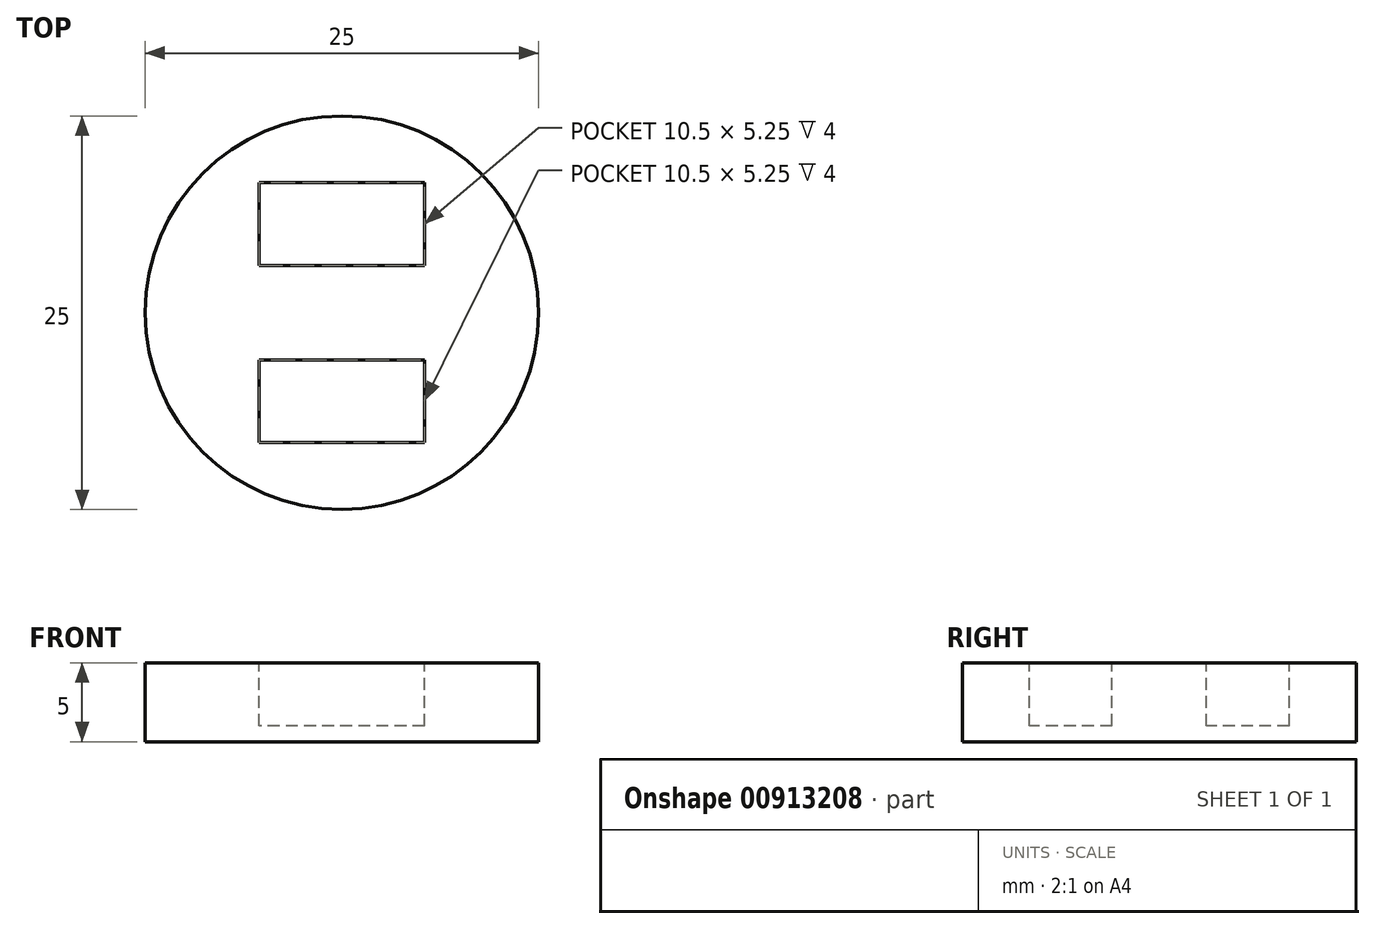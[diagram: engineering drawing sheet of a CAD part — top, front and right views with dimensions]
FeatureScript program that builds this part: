
annotation { "Feature Type Name" : "Feature", "Feature Type Description" : "" }
export const myFeature = defineFeature(function(context is Context, id is Id, definition is map)
    precondition{}
    {
        {
            var Q0;
            Q0=qCreatedBy(makeId("Top.planeOp"),FACE);
            var sketch = newSketch(context, id + "F0", { "sketchPlane" : qUnion([Q0])});
            skCircle(sketch, "E0", {"center": v(0, 0) * mm, "radius": 12.5 * mm});
            skSolve(sketch);
        }
        {
            var Q0;
            Q0=qSketchRegion(id+"F0",true);
            extrude(context, id + "F1", {"entities" : qUnion([Q0]), "depth" : 5 * mm, "offsetDistance" : 25 * mm});
        }
        {
            var Q0;
            Q0=makeQuery(id+"F1.opExtrude","CAP_FACE",FACE,{"disambiguationData":[OSD([sQuery(id+"F0.wireOp",EDGE,"E0")])],"isStart":false});
            var sketch = newSketch(context, id + "F2", { "sketchPlane" : qUnion([Q0])});
            skLineSegment(sketch, "E1.bottom", {"start": v(5.25, 8.25) * mm, "end": v(-5.25, 8.25) * mm});
            skLineSegment(sketch, "E1.top", {"start": v(5.25, 3) * mm, "end": v(-5.25, 3) * mm});
            skLineSegment(sketch, "E1.left", {"start": v(5.25, 8.25) * mm, "end": v(5.25, 3) * mm});
            skLineSegment(sketch, "E1.right", {"start": v(-5.25, 8.25) * mm, "end": v(-5.25, 3) * mm});
            skPoint(sketch, "E1.middle", {"position": v(0, 5.62) * mm});
            skLineSegment(sketch, "E2.bottom", {"start": v(5.25, -3) * mm, "end": v(-5.25, -3) * mm});
            skLineSegment(sketch, "E2.top", {"start": v(5.25, -8.25) * mm, "end": v(-5.25, -8.25) * mm});
            skLineSegment(sketch, "E2.left", {"start": v(5.25, -3) * mm, "end": v(5.25, -8.25) * mm});
            skLineSegment(sketch, "E2.right", {"start": v(-5.25, -3) * mm, "end": v(-5.25, -8.25) * mm});
            skPoint(sketch, "E2.middle", {"position": v(0, -5.62) * mm});
            skSolve(sketch);
        }
        {
            var Q0;
            Q0=qSketchRegion(id+"F2",true);
            extrude(context, id + "F3", {"entities" : qUnion([Q0]), "depth" : -4 * mm, "offsetDistance" : 25 * mm});
        }
        {
            var Q0;
            Q0=makeQuery(id+"F3.opExtrude","SWEPT_BODY",BODY,{"disambiguationData":[OSD([sQuery(id+"F2.wireOp",EDGE,"E2.bottom"),sQuery(id+"F2.wireOp",EDGE,"E2.top"),sQuery(id+"F2.wireOp",EDGE,"E2.left"),sQuery(id+"F2.wireOp",EDGE,"E2.right")])]});
            var Q1;
            Q1=makeQuery(id+"F3.opExtrude","SWEPT_BODY",BODY,{"disambiguationData":[OSD([sQuery(id+"F2.wireOp",EDGE,"E1.bottom"),sQuery(id+"F2.wireOp",EDGE,"E1.top"),sQuery(id+"F2.wireOp",EDGE,"E1.left"),sQuery(id+"F2.wireOp",EDGE,"E1.right")])]});
            var Q2;
            Q2=makeQuery(id+"F1.opExtrude","SWEPT_BODY",BODY,{"disambiguationData":[OSD([sQuery(id+"F0.wireOp",EDGE,"E0")])]});
            booleanBodies(context, id + "F4", {"operationType" : BooleanOperationType.SUBTRACTION, "tools" : qUnion([Q0, Q1]), "targets" : qUnion([Q2])});
        }
    });
